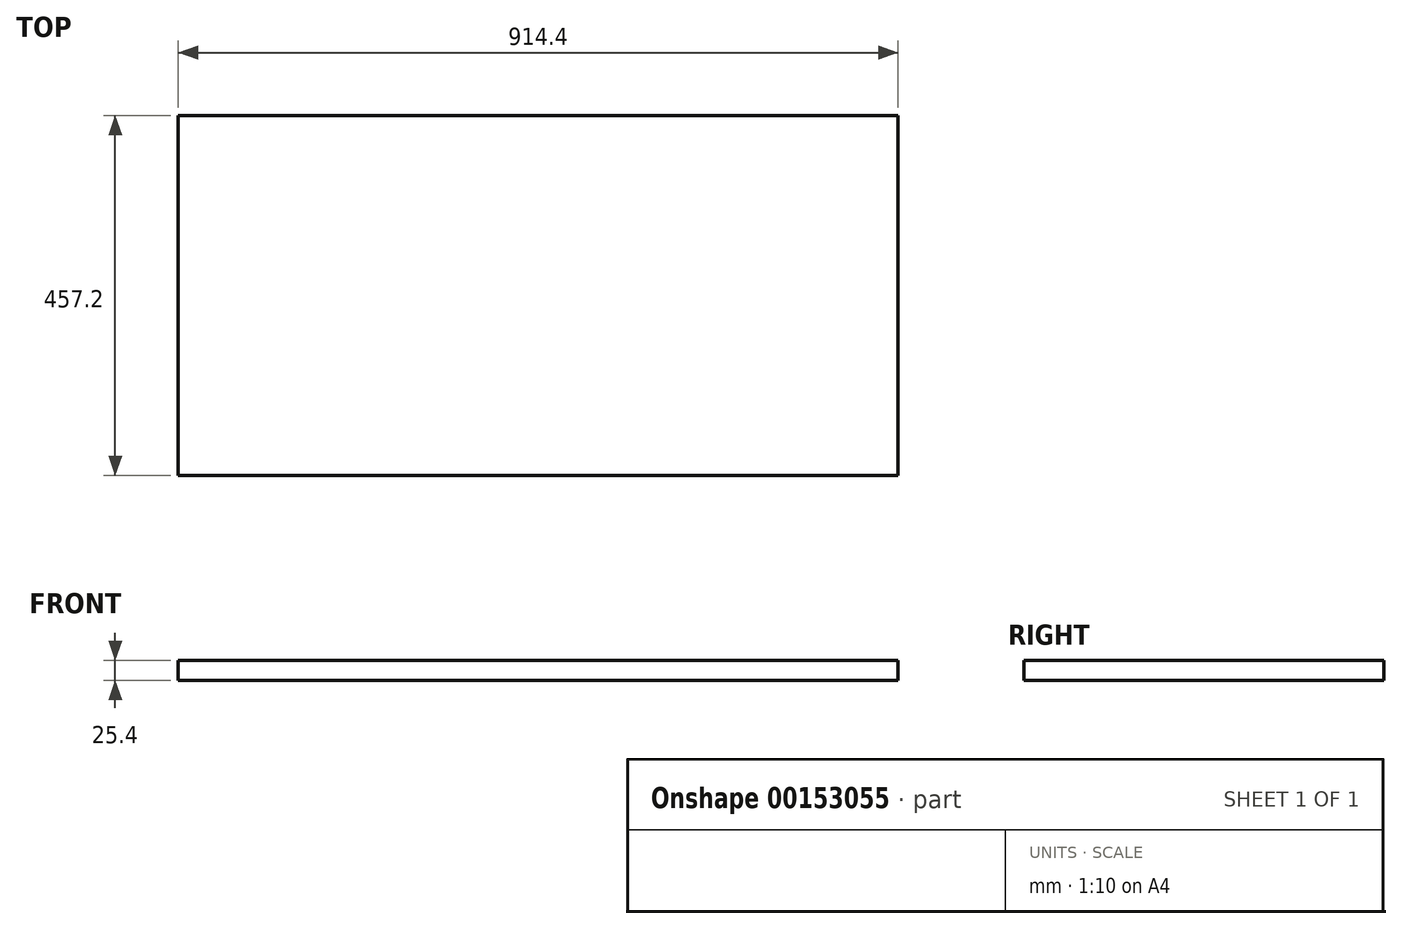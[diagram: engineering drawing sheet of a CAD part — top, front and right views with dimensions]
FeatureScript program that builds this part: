
annotation { "Feature Type Name" : "Feature", "Feature Type Description" : "" }
export const myFeature = defineFeature(function(context is Context, id is Id, definition is map)
    precondition{}
    {
        {
            var Q0;
            Q0=qCreatedBy(makeId("Top.planeOp"),FACE);
            var sketch = newSketch(context, id + "F0", { "sketchPlane" : qUnion([Q0])});
            skLineSegment(sketch, "E0.bottom", {"start": v(0, 0) * mm, "end": v(914.4, 0) * mm});
            skLineSegment(sketch, "E0.top", {"start": v(0, 457.2) * mm, "end": v(914.4, 457.2) * mm});
            skLineSegment(sketch, "E0.left", {"start": v(0, 0) * mm, "end": v(0, 457.2) * mm});
            skLineSegment(sketch, "E0.right", {"start": v(914.4, 0) * mm, "end": v(914.4, 457.2) * mm});
            skSolve(sketch);
        }
        {
            var Q0;
            Q0=makeQuery(id+"F0.imprint","IMPRINT",FACE,{"disambiguationData":[TD([[makeQuery(id+"F0.imprint","IMPRINT",EDGE,{"derivedFrom":sQuery(id+"F0.wireOp",EDGE,"E0.bottom")}),1.0]])]});
            extrude(context, id + "F1", {"entities" : qUnion([Q0]), "depth" : 25.4 * mm});
        }
    });
